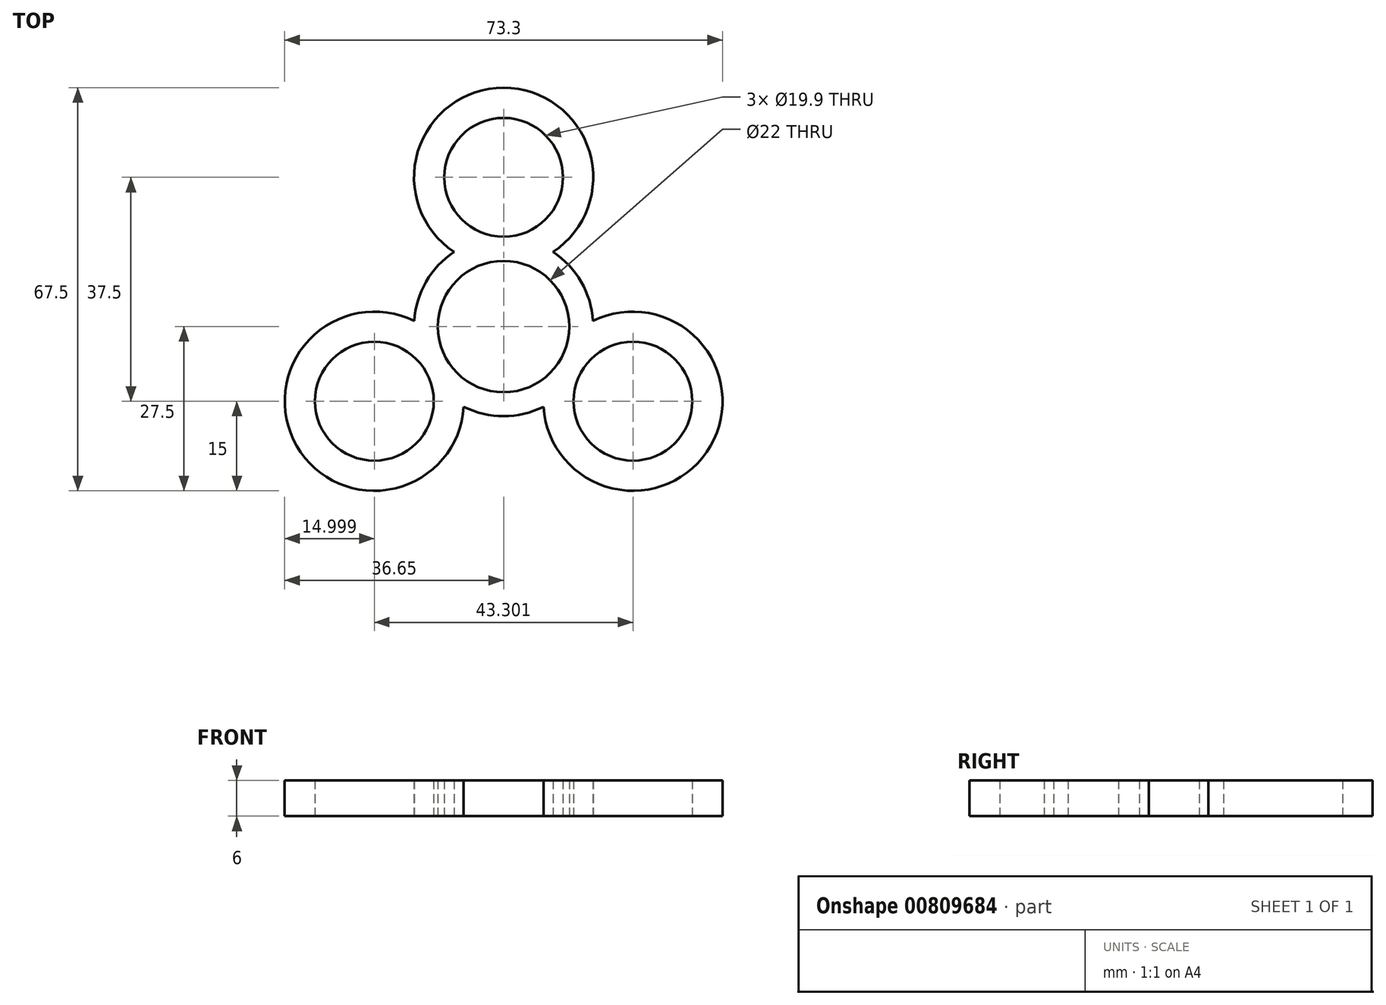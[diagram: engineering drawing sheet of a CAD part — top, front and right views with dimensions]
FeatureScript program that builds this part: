
annotation { "Feature Type Name" : "Feature", "Feature Type Description" : "" }
export const myFeature = defineFeature(function(context is Context, id is Id, definition is map)
    precondition{}
    {
        {
            var Q0;
            Q0=qCreatedBy(makeId("Top.planeOp"),FACE);
            var sketch = newSketch(context, id + "F0", { "sketchPlane" : qUnion([Q0])});
            skArc(sketch, "E0", {"start": v(9.53, 5.5) * mm, "mid": v(0, 11) * mm, "end": v(-9.53, 5.5) * mm});
            skLineSegment(sketch, "E1", {"start": v(0, 0) * mm, "end": v(0, 25) * mm});
            skCircle(sketch, "E2", {"center": v(0, 25) * mm, "radius": 9.95 * mm});
            skArc(sketch, "E3", {"start": v(-8.3, 12.5) * mm, "mid": v(-10.93, 10.27) * mm, "end": v(-13, 7.5) * mm});
            skArc(sketch, "E4", {"start": v(8.3, 12.5) * mm, "mid": v(0, 40) * mm, "end": v(-8.3, 12.5) * mm});
            skArc(sketch, "E5.trimOffspring", {"start": v(13, 7.5) * mm, "mid": v(10.93, 10.27) * mm, "end": v(8.3, 12.5) * mm});
            skCircle(sketch, "E6.1.0", {"center": v(-21.65, -12.5) * mm, "radius": 9.95 * mm});
            skArc(sketch, "E6.1.1", {"start": v(-14.97, 0.93) * mm, "mid": v(-34.64, -20) * mm, "end": v(-6.68, -13.43) * mm});
            skArc(sketch, "E6.1.2", {"start": v(-9.53, 5.5) * mm, "mid": v(-9.53, -5.5) * mm, "end": v(0, -11) * mm});
            skArc(sketch, "E6.1.3", {"start": v(-13, 7.5) * mm, "mid": v(-14.36, 4.33) * mm, "end": v(-14.97, 0.93) * mm});
            skArc(sketch, "E6.1.4", {"start": v(-6.68, -13.43) * mm, "mid": v(-3.43, -14.6) * mm, "end": v(0, -15) * mm});
            skCircle(sketch, "E6.2.0", {"center": v(21.65, -12.5) * mm, "radius": 9.95 * mm});
            skArc(sketch, "E6.2.1", {"start": v(6.68, -13.43) * mm, "mid": v(34.64, -20) * mm, "end": v(14.97, 0.93) * mm});
            skArc(sketch, "E6.2.2", {"start": v(0, -11) * mm, "mid": v(9.53, -5.5) * mm, "end": v(9.53, 5.5) * mm});
            skArc(sketch, "E6.2.3", {"start": v(0, -15) * mm, "mid": v(3.43, -14.6) * mm, "end": v(6.68, -13.43) * mm});
            skArc(sketch, "E6.2.4", {"start": v(14.97, 0.93) * mm, "mid": v(14.36, 4.33) * mm, "end": v(13, 7.5) * mm});
            skSolve(sketch);
        }
        {
            var Q0;
            Q0 = qSketchRegion(id + "FX4xlb0EuypCNPd_0", true);
            var Q1;
            Q1=makeQuery(id+"F0.imprint","IMPRINT",FACE,{"disambiguationData":[TD([[makeQuery(id+"F0.imprint","IMPRINT",EDGE,{"derivedFrom":sQuery(id+"F0.wireOp",EDGE,"E2")}),-1.0]])]});
            extrude(context, id + "F1", {"entities" : qUnion([Q0, Q1]), "depth" : 6 * mm, "offsetDistance" : 25 * mm});
        }
    });
